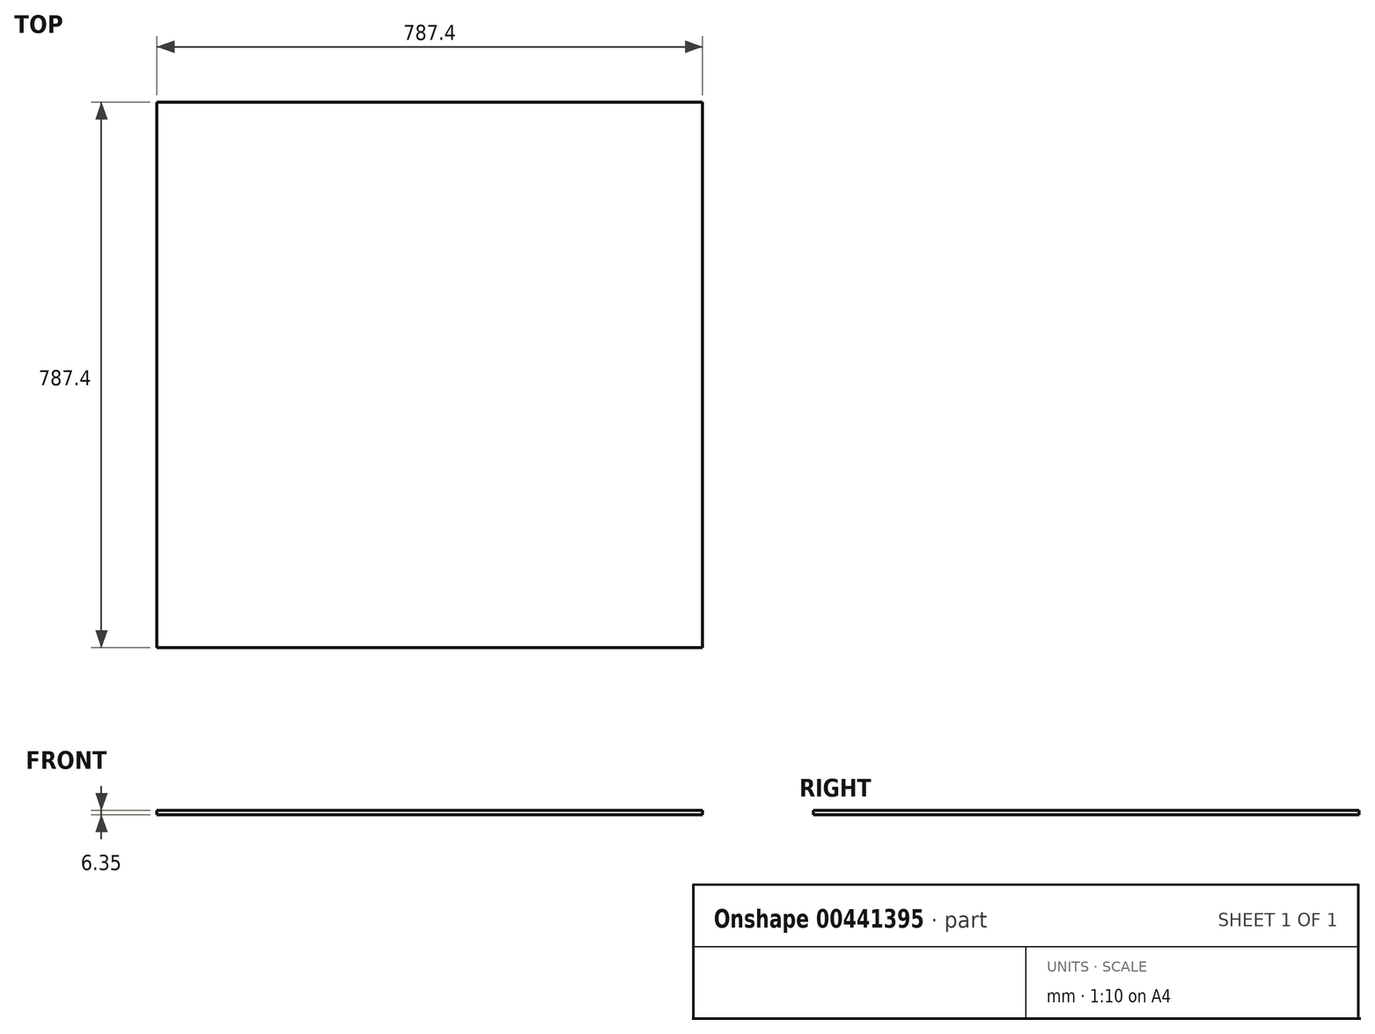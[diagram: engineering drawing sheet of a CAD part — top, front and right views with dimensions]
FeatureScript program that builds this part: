
annotation { "Feature Type Name" : "Feature", "Feature Type Description" : "" }
export const myFeature = defineFeature(function(context is Context, id is Id, definition is map)
    precondition{}
    {
        {
            var Q0;
            Q0=qCreatedBy(makeId("Top.planeOp"),FACE);
            var sketch = newSketch(context, id + "F0", { "sketchPlane" : qUnion([Q0])});
            skLineSegment(sketch, "E0.bottom", {"start": v(-393.7, 393.7) * mm, "end": v(393.7, 393.7) * mm});
            skLineSegment(sketch, "E0.top", {"start": v(-393.7, -393.7) * mm, "end": v(393.7, -393.7) * mm});
            skLineSegment(sketch, "E0.left", {"start": v(-393.7, 393.7) * mm, "end": v(-393.7, -393.7) * mm});
            skLineSegment(sketch, "E0.right", {"start": v(393.7, 393.7) * mm, "end": v(393.7, -393.7) * mm});
            skPoint(sketch, "E0.middle", {"position": v(0, 0) * mm});
            skSolve(sketch);
        }
        {
            var Q0;
            Q0 = qSketchRegion(id + "F0", true);
            extrude(context, id + "F1", {"entities" : qUnion([Q0]), "depth" : 6.35 * mm});
        }
    });
